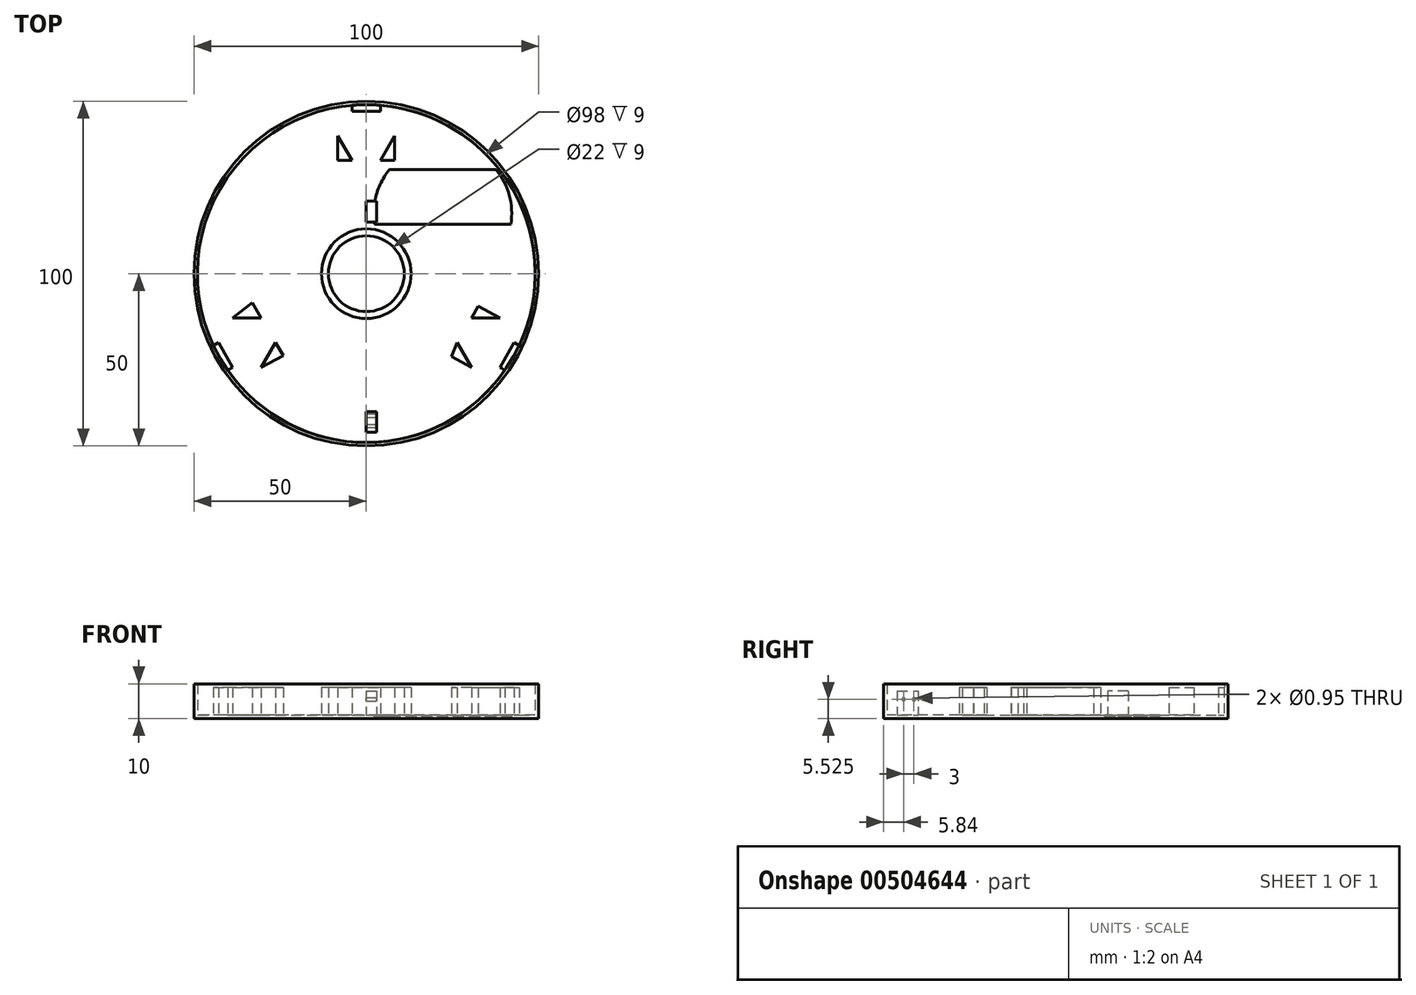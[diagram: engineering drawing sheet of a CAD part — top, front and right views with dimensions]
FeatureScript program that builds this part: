
annotation { "Feature Type Name" : "Feature", "Feature Type Description" : "" }
export const myFeature = defineFeature(function(context is Context, id is Id, definition is map)
    precondition{}
    {
        {
            var Q0;
            Q0=qCreatedBy(makeId("Top.planeOp"),FACE);
            var sketch = newSketch(context, id + "F0", { "sketchPlane" : qUnion([Q0])});
            skCircle(sketch, "E0", {"center": v(0, 0) * mm, "radius": 11 * mm});
            skCircle(sketch, "E1", {"center": v(0, 0) * mm, "radius": 13 * mm});
            skCircle(sketch, "E2", {"center": v(0, 0) * mm, "radius": 50 * mm});
            skCircle(sketch, "E3", {"center": v(0, 0) * mm, "radius": 49 * mm});
            skLineSegment(sketch, "E4.0", {"start": v(113.43, -65.49) * mm, "end": v(-113.43, -65.49) * mm});
            skLineSegment(sketch, "E4.1", {"start": v(-113.43, -65.49) * mm, "end": v(0, 130.97) * mm});
            skLineSegment(sketch, "E4.2", {"start": v(0, 130.97) * mm, "end": v(113.43, -65.49) * mm});
            skPoint(sketch, "E4.0.midPoint", {"position": v(0, -65.49) * mm});
            skLineSegment(sketch, "E5", {"start": v(0, 0) * mm, "end": v(0, 130.97) * mm});
            skLineSegment(sketch, "E6", {"start": v(0, 0) * mm, "end": v(-113.43, -65.49) * mm});
            skLineSegment(sketch, "E7", {"start": v(113.43, -65.49) * mm, "end": v(0, 0) * mm});
            skCircle(sketch, "E8.cCircle", {"center": v(0, 40) * mm, "radius": 7.15 * mm, "construction": true});
            skLineSegment(sketch, "E8.0", {"start": v(4.13, 32.85) * mm, "end": v(-4.13, 32.85) * mm});
            skLineSegment(sketch, "E8.1", {"start": v(-4.13, 32.85) * mm, "end": v(-8.26, 40) * mm});
            skLineSegment(sketch, "E8.2", {"start": v(-8.26, 40) * mm, "end": v(-4.13, 47.15) * mm});
            skLineSegment(sketch, "E8.3", {"start": v(-4.13, 47.15) * mm, "end": v(4.13, 47.15) * mm});
            skLineSegment(sketch, "E8.4", {"start": v(4.13, 47.15) * mm, "end": v(8.26, 40) * mm});
            skLineSegment(sketch, "E8.5", {"start": v(8.26, 40) * mm, "end": v(4.13, 32.85) * mm});
            skPoint(sketch, "E8.0.midPoint", {"position": v(0, 32.85) * mm});
            skCircle(sketch, "E9.cCircle", {"center": v(-34.64, -20) * mm, "radius": 7.15 * mm, "construction": true});
            skLineSegment(sketch, "E9.0", {"start": v(-30.51, -12.85) * mm, "end": v(-26.38, -20) * mm});
            skLineSegment(sketch, "E9.1", {"start": v(-26.38, -20) * mm, "end": v(-30.51, -27.15) * mm});
            skLineSegment(sketch, "E9.2", {"start": v(-30.51, -27.15) * mm, "end": v(-38.77, -27.15) * mm});
            skLineSegment(sketch, "E9.3", {"start": v(-38.77, -27.15) * mm, "end": v(-42.9, -20) * mm});
            skLineSegment(sketch, "E9.4", {"start": v(-42.9, -20) * mm, "end": v(-38.77, -12.85) * mm});
            skLineSegment(sketch, "E9.5", {"start": v(-38.77, -12.85) * mm, "end": v(-30.51, -12.85) * mm});
            skPoint(sketch, "E9.0.midPoint", {"position": v(-28.45, -16.43) * mm});
            skCircle(sketch, "E10.cCircle", {"center": v(34.64, -20) * mm, "radius": 7.15 * mm, "construction": true});
            skLineSegment(sketch, "E10.0", {"start": v(26.38, -20) * mm, "end": v(30.51, -12.85) * mm});
            skLineSegment(sketch, "E10.1", {"start": v(30.51, -12.85) * mm, "end": v(38.77, -12.85) * mm});
            skLineSegment(sketch, "E10.2", {"start": v(38.77, -12.85) * mm, "end": v(42.9, -20) * mm});
            skLineSegment(sketch, "E10.3", {"start": v(42.9, -20) * mm, "end": v(38.77, -27.15) * mm});
            skLineSegment(sketch, "E10.4", {"start": v(38.77, -27.15) * mm, "end": v(30.51, -27.15) * mm});
            skLineSegment(sketch, "E10.5", {"start": v(30.51, -27.15) * mm, "end": v(26.38, -20) * mm});
            skPoint(sketch, "E10.0.midPoint", {"position": v(28.45, -16.43) * mm});
            skLineSegment(sketch, "E11", {"start": v(-4.13, 47.15) * mm, "end": v(-4.13, 48.83) * mm});
            skLineSegment(sketch, "E12", {"start": v(4.13, 47.15) * mm, "end": v(4.13, 48.83) * mm});
            skLineSegment(sketch, "E13", {"start": v(-8.26, 40) * mm, "end": v(-8.26, 32.85) * mm});
            skLineSegment(sketch, "E14", {"start": v(-8.26, 32.85) * mm, "end": v(-4.13, 32.85) * mm});
            skLineSegment(sketch, "E15", {"start": v(8.26, 40) * mm, "end": v(8.26, 32.85) * mm});
            skLineSegment(sketch, "E16", {"start": v(8.26, 32.85) * mm, "end": v(4.13, 32.85) * mm});
            skLineSegment(sketch, "E17", {"start": v(42.9, -20) * mm, "end": v(44.35, -20.84) * mm});
            skLineSegment(sketch, "E18", {"start": v(38.77, -27.15) * mm, "end": v(40.22, -27.99) * mm});
            skLineSegment(sketch, "E19", {"start": v(30.51, -12.85) * mm, "end": v(32.52, -9.37) * mm});
            skLineSegment(sketch, "E20", {"start": v(32.52, -9.37) * mm, "end": v(38.77, -12.85) * mm});
            skLineSegment(sketch, "E21", {"start": v(30.51, -27.15) * mm, "end": v(24.65, -24) * mm});
            skLineSegment(sketch, "E22", {"start": v(24.65, -24) * mm, "end": v(26.38, -20) * mm});
            skLineSegment(sketch, "E23", {"start": v(-42.9, -20) * mm, "end": v(-44.35, -20.84) * mm});
            skLineSegment(sketch, "E24", {"start": v(-38.77, -27.15) * mm, "end": v(-40.22, -27.99) * mm});
            skLineSegment(sketch, "E25", {"start": v(-26.38, -20) * mm, "end": v(-24.13, -23.82) * mm});
            skLineSegment(sketch, "E26", {"start": v(-24.13, -23.82) * mm, "end": v(-30.51, -27.15) * mm});
            skLineSegment(sketch, "E27", {"start": v(-30.51, -12.85) * mm, "end": v(-33.07, -8.43) * mm});
            skLineSegment(sketch, "E28", {"start": v(-33.07, -8.43) * mm, "end": v(-38.77, -12.85) * mm});
            skSolve(sketch);
        }
        {
            var Q0;
            Q0=makeQuery(id+"F0.imprint","IMPRINT",FACE,{"disambiguationData":[TD([[makeQuery(id+"F0.imprint","IMPRINT",EDGE,{"derivedFrom":sQuery(id+"F0.wireOp",EDGE,"E2")}),1.0]])]});
            extrude(context, id + "F1", {"entities" : qUnion([Q0]), "depth" : 10 * mm, "offsetDistance" : 25 * mm});
        }
        {
            var Q0;
            Q0=makeQuery(id+"F0.imprint","IMPRINT",FACE,{"disambiguationData":[TD([[makeQuery(id+"F0.imprint","IMPRINT",EDGE,{"derivedFrom":sQuery(id+"F0.wireOp",EDGE,"E1")}),-1.0]])]});
            var Q1;
            {var subQ0=sQuery(id+"F0.wireOp",EDGE,"E9.4");Q1=makeQuery(id+"F0.imprint","IMPRINT",FACE,{"disambiguationData":[TD([[makeQuery(id+"F0.imprint","IMPRINT",EDGE,{"derivedFrom":subQ0}),-1.0]])]});}
            var Q2;
            {var subQ6=sQuery(id+"F0.wireOp",EDGE,"E9.1");Q2=makeQuery(id+"F0.imprint","IMPRINT",FACE,{"disambiguationData":[TD([[makeQuery(id+"F0.imprint","IMPRINT",EDGE,{"derivedFrom":subQ6}),-1.0]])]});}
            var Q3;
            {var subQ1=sQuery(id+"F0.wireOp",EDGE,"E10.1");Q3=makeQuery(id+"F0.imprint","IMPRINT",FACE,{"disambiguationData":[TD([[makeQuery(id+"F0.imprint","IMPRINT",EDGE,{"derivedFrom":subQ1}),-1.0]])]});}
            var Q4;
            {var subQ0=sQuery(id+"F0.wireOp",EDGE,"E10.4");Q4=makeQuery(id+"F0.imprint","IMPRINT",FACE,{"disambiguationData":[TD([[makeQuery(id+"F0.imprint","IMPRINT",EDGE,{"derivedFrom":subQ0}),-1.0]])]});}
            var Q5;
            {var subQ0=sQuery(id+"F0.wireOp",EDGE,"E8.4");Q5=makeQuery(id+"F0.imprint","IMPRINT",FACE,{"disambiguationData":[TD([[makeQuery(id+"F0.imprint","IMPRINT",EDGE,{"derivedFrom":subQ0}),-1.0]])]});}
            var Q6;
            {var subQ1=sQuery(id+"F0.wireOp",EDGE,"E8.1");Q6=makeQuery(id+"F0.imprint","IMPRINT",FACE,{"disambiguationData":[TD([[makeQuery(id+"F0.imprint","IMPRINT",EDGE,{"derivedFrom":subQ1}),-1.0]])]});}
            extrude(context, id + "F2", {"entities" : qUnion([Q0, Q1, Q2, Q3, Q4, Q5, Q6]), "operationType" : NewBodyOperationType.ADD, "depth" : 1 * mm, "offsetDistance" : 25 * mm});
        }
        {
            var Q0;
            Q0=makeQuery(id+"F0.imprint","IMPRINT",FACE,{"disambiguationData":[TD([[makeQuery(id+"F0.imprint","IMPRINT",EDGE,{"derivedFrom":sQuery(id+"F0.wireOp",EDGE,"E0")}),-1.0]])]});
            var Q1;
            Q1=makeQuery(id+"F0.imprint","IMPRINT",FACE,{"disambiguationData":[TD([[makeQuery(id+"F0.imprint","IMPRINT",EDGE,{"derivedFrom":sQuery(id+"F0.wireOp",EDGE,"E9.1")}),1.0]])]});
            var Q2;
            {var subQ0=sQuery(id+"F0.wireOp",EDGE,"E24");Q2=makeQuery(id+"F0.imprint","IMPRINT",FACE,{"disambiguationData":[TD([[makeQuery(id+"F0.imprint","IMPRINT",EDGE,{"derivedFrom":subQ0}),-1.0]])]});}
            var Q3;
            {var subQ0=sQuery(id+"F0.wireOp",EDGE,"E23");Q3=makeQuery(id+"F0.imprint","IMPRINT",FACE,{"disambiguationData":[TD([[makeQuery(id+"F0.imprint","IMPRINT",EDGE,{"derivedFrom":subQ0}),1.0]])]});}
            var Q4;
            Q4=makeQuery(id+"F0.imprint","IMPRINT",FACE,{"disambiguationData":[TD([[makeQuery(id+"F0.imprint","IMPRINT",EDGE,{"derivedFrom":sQuery(id+"F0.wireOp",EDGE,"E9.5")}),1.0]])]});
            var Q5;
            Q5=makeQuery(id+"F0.imprint","IMPRINT",FACE,{"disambiguationData":[TD([[makeQuery(id+"F0.imprint","IMPRINT",EDGE,{"derivedFrom":sQuery(id+"F0.wireOp",EDGE,"E8.5")}),1.0]])]});
            var Q6;
            Q6=makeQuery(id+"F0.imprint","IMPRINT",FACE,{"disambiguationData":[TD([[makeQuery(id+"F0.imprint","IMPRINT",EDGE,{"derivedFrom":sQuery(id+"F0.wireOp",EDGE,"E8.1")}),1.0]])]});
            var Q7;
            {var subQ0=sQuery(id+"F0.wireOp",EDGE,"E12");Q7=makeQuery(id+"F0.imprint","IMPRINT",FACE,{"disambiguationData":[TD([[makeQuery(id+"F0.imprint","IMPRINT",EDGE,{"derivedFrom":subQ0}),1.0]])]});}
            var Q8;
            {var subQ0=sQuery(id+"F0.wireOp",EDGE,"E11");Q8=makeQuery(id+"F0.imprint","IMPRINT",FACE,{"disambiguationData":[TD([[makeQuery(id+"F0.imprint","IMPRINT",EDGE,{"derivedFrom":subQ0}),-1.0]])]});}
            var Q9;
            Q9=makeQuery(id+"F0.imprint","IMPRINT",FACE,{"disambiguationData":[TD([[makeQuery(id+"F0.imprint","IMPRINT",EDGE,{"derivedFrom":sQuery(id+"F0.wireOp",EDGE,"E10.5")}),1.0]])]});
            var Q10;
            Q10=makeQuery(id+"F0.imprint","IMPRINT",FACE,{"disambiguationData":[TD([[makeQuery(id+"F0.imprint","IMPRINT",EDGE,{"derivedFrom":sQuery(id+"F0.wireOp",EDGE,"E10.1")}),1.0]])]});
            var Q11;
            {var subQ0=sQuery(id+"F0.wireOp",EDGE,"E17");Q11=makeQuery(id+"F0.imprint","IMPRINT",FACE,{"disambiguationData":[TD([[makeQuery(id+"F0.imprint","IMPRINT",EDGE,{"derivedFrom":subQ0}),-1.0]])]});}
            var Q12;
            {var subQ0=sQuery(id+"F0.wireOp",EDGE,"E18");Q12=makeQuery(id+"F0.imprint","IMPRINT",FACE,{"disambiguationData":[TD([[makeQuery(id+"F0.imprint","IMPRINT",EDGE,{"derivedFrom":subQ0}),1.0]])]});}
            extrude(context, id + "F3", {"entities" : qUnion([Q0, Q1, Q2, Q3, Q4, Q5, Q6, Q7, Q8, Q9, Q10, Q11, Q12]), "operationType" : NewBodyOperationType.ADD, "depth" : 9 * mm, "offsetDistance" : 25 * mm});
        }
        {
            var Q0;
            Q0=makeQuery(id+"F2.opExtrude","CAP_FACE",FACE,{"disambiguationData":[OSD([sQuery(id+"F0.wireOp",EDGE,"E1"),sQuery(id+"F0.wireOp",EDGE,"E3"),sQuery(id+"F0.wireOp",EDGE,"E8.1"),sQuery(id+"F0.wireOp",EDGE,"E8.3"),sQuery(id+"F0.wireOp",EDGE,"E8.5"),sQuery(id+"F0.wireOp",EDGE,"E9.1"),sQuery(id+"F0.wireOp",EDGE,"E9.3"),sQuery(id+"F0.wireOp",EDGE,"E9.5"),sQuery(id+"F0.wireOp",EDGE,"E10.1"),sQuery(id+"F0.wireOp",EDGE,"E10.3"),sQuery(id+"F0.wireOp",EDGE,"E10.5"),sQuery(id+"F0.wireOp",EDGE,"E11"),sQuery(id+"F0.wireOp",EDGE,"E12"),sQuery(id+"F0.wireOp",EDGE,"E13"),sQuery(id+"F0.wireOp",EDGE,"E14"),sQuery(id+"F0.wireOp",EDGE,"E15"),sQuery(id+"F0.wireOp",EDGE,"E16"),sQuery(id+"F0.wireOp",EDGE,"E17"),sQuery(id+"F0.wireOp",EDGE,"E18"),sQuery(id+"F0.wireOp",EDGE,"E19"),sQuery(id+"F0.wireOp",EDGE,"E20"),sQuery(id+"F0.wireOp",EDGE,"E21"),sQuery(id+"F0.wireOp",EDGE,"E22"),sQuery(id+"F0.wireOp",EDGE,"E23"),sQuery(id+"F0.wireOp",EDGE,"E24"),sQuery(id+"F0.wireOp",EDGE,"E25"),sQuery(id+"F0.wireOp",EDGE,"E26"),sQuery(id+"F0.wireOp",EDGE,"E27"),sQuery(id+"F0.wireOp",EDGE,"E28")])],"isStart":false});
            var sketch = newSketch(context, id + "F4", { "sketchPlane" : qUnion([Q0])});
            skLineSegment(sketch, "E29.bottom", {"start": v(0, -46) * mm, "end": v(3, -46) * mm});
            skLineSegment(sketch, "E29.top", {"start": v(0, -40) * mm, "end": v(3, -40) * mm});
            skLineSegment(sketch, "E29.left", {"start": v(0, -46) * mm, "end": v(0, -40) * mm});
            skLineSegment(sketch, "E29.right", {"start": v(3, -46) * mm, "end": v(3, -40) * mm});
            skLineSegment(sketch, "E30.bottom", {"start": v(0, 21) * mm, "end": v(3, 21) * mm});
            skLineSegment(sketch, "E30.top", {"start": v(0, 15) * mm, "end": v(3, 15) * mm});
            skLineSegment(sketch, "E30.left", {"start": v(0, 21) * mm, "end": v(0, 15) * mm});
            skLineSegment(sketch, "E30.right", {"start": v(3, 21) * mm, "end": v(3, 15) * mm});
            skSolve(sketch);
        }
        {
            var Q0;
            Q0=makeQuery(id+"F4.imprint","IMPRINT",FACE,{"disambiguationData":[TD([[makeQuery(id+"F4.imprint","IMPRINT",EDGE,{"derivedFrom":sQuery(id+"F4.wireOp",EDGE,"E29.bottom")}),1.0]])]});
            var Q1;
            Q1=makeQuery(id+"F4.imprint","IMPRINT",FACE,{"disambiguationData":[TD([[makeQuery(id+"F4.imprint","IMPRINT",EDGE,{"derivedFrom":sQuery(id+"F4.wireOp",EDGE,"E30.bottom")}),-1.0]])]});
            extrude(context, id + "F5", {"entities" : qUnion([Q0, Q1]), "operationType" : NewBodyOperationType.ADD, "depth" : 7 * mm, "offsetDistance" : 25 * mm});
        }
        {
            var Q0;
            Q0=makeQuery(id+"F5.opExtrude","SWEPT_FACE",FACE,{"disambiguationData":[OSD([sQuery(id+"F4.wireOp",EDGE,"E29.right")])]});
            var sketch = newSketch(context, id + "F6", { "sketchPlane" : qUnion([Q0])});
            skCircle(sketch, "E31", {"center": v(-41.16, 5.53) * mm, "radius": 0.48 * mm});
            skCircle(sketch, "E32", {"center": v(-44.16, 5.53) * mm, "radius": 0.47 * mm});
            skSolve(sketch);
        }
        {
            var Q0;
            Q0=makeQuery(id+"F5.opExtrude","SWEPT_FACE",FACE,{"disambiguationData":[OSD([sQuery(id+"F4.wireOp",EDGE,"E30.right")])]});
            var sketch = newSketch(context, id + "F7", { "sketchPlane" : qUnion([Q0])});
            skCircle(sketch, "E33", {"center": v(26.47, 6.58) * mm, "radius": 0.47 * mm});
            skCircle(sketch, "E34", {"center": v(29.47, 6.58) * mm, "radius": 0.47 * mm});
            skSolve(sketch);
        }
        {
            var Q0;
            Q0=makeQuery(id+"F7.imprint","IMPRINT",FACE,{"disambiguationData":[TD([[makeQuery(id+"F7.imprint","IMPRINT",EDGE,{"derivedFrom":sQuery(id+"F7.wireOp",EDGE,"E33")}),1.0]])]});
            var Q1;
            Q1=makeQuery(id+"F7.imprint","IMPRINT",FACE,{"disambiguationData":[TD([[makeQuery(id+"F7.imprint","IMPRINT",EDGE,{"derivedFrom":sQuery(id+"F7.wireOp",EDGE,"E34")}),1.0]])]});
            var Q2;
            Q2=makeQuery(id+"F6.imprint","IMPRINT",FACE,{"disambiguationData":[TD([[makeQuery(id+"F6.imprint","IMPRINT",EDGE,{"derivedFrom":sQuery(id+"F6.wireOp",EDGE,"E32")}),1.0]])]});
            var Q3;
            Q3=makeQuery(id+"F6.imprint","IMPRINT",FACE,{"disambiguationData":[TD([[makeQuery(id+"F6.imprint","IMPRINT",EDGE,{"derivedFrom":sQuery(id+"F6.wireOp",EDGE,"E31")}),1.0]])]});
            extrude(context, id + "F8", {"entities" : qUnion([Q0, Q1, Q2, Q3]), "operationType" : NewBodyOperationType.REMOVE, "oppositeDirection" : true, "depth" : 3 * mm, "offsetDistance" : 25 * mm});
        }
        {
            var Q0;
            Q0=makeQuery(id+"F2.opExtrude","CAP_FACE",FACE,{"disambiguationData":[OSD([sQuery(id+"F0.wireOp",EDGE,"E1"),sQuery(id+"F0.wireOp",EDGE,"E3"),sQuery(id+"F0.wireOp",EDGE,"E8.1"),sQuery(id+"F0.wireOp",EDGE,"E8.3"),sQuery(id+"F0.wireOp",EDGE,"E8.5"),sQuery(id+"F0.wireOp",EDGE,"E9.1"),sQuery(id+"F0.wireOp",EDGE,"E9.3"),sQuery(id+"F0.wireOp",EDGE,"E9.5"),sQuery(id+"F0.wireOp",EDGE,"E10.1"),sQuery(id+"F0.wireOp",EDGE,"E10.3"),sQuery(id+"F0.wireOp",EDGE,"E10.5"),sQuery(id+"F0.wireOp",EDGE,"E11"),sQuery(id+"F0.wireOp",EDGE,"E12"),sQuery(id+"F0.wireOp",EDGE,"E13"),sQuery(id+"F0.wireOp",EDGE,"E14"),sQuery(id+"F0.wireOp",EDGE,"E15"),sQuery(id+"F0.wireOp",EDGE,"E16"),sQuery(id+"F0.wireOp",EDGE,"E17"),sQuery(id+"F0.wireOp",EDGE,"E18"),sQuery(id+"F0.wireOp",EDGE,"E19"),sQuery(id+"F0.wireOp",EDGE,"E20"),sQuery(id+"F0.wireOp",EDGE,"E21"),sQuery(id+"F0.wireOp",EDGE,"E22"),sQuery(id+"F0.wireOp",EDGE,"E23"),sQuery(id+"F0.wireOp",EDGE,"E24"),sQuery(id+"F0.wireOp",EDGE,"E25"),sQuery(id+"F0.wireOp",EDGE,"E26"),sQuery(id+"F0.wireOp",EDGE,"E27"),sQuery(id+"F0.wireOp",EDGE,"E28")])],"isStart":false});
            var sketch = newSketch(context, id + "F9", { "sketchPlane" : qUnion([Q0])});
            skLineSegment(sketch, "E35.bottom", {"start": v(2.48, 21.05) * mm, "end": v(-7.02, 21.05) * mm});
            skLineSegment(sketch, "E35.top", {"start": v(2.48, 28.55) * mm, "end": v(-7.02, 28.55) * mm});
            skLineSegment(sketch, "E35.left", {"start": v(2.48, 21.05) * mm, "end": v(2.48, 28.55) * mm});
            skLineSegment(sketch, "E35.right", {"start": v(-7.02, 21.05) * mm, "end": v(-7.02, 28.55) * mm});
            skCircle(sketch, "E36", {"center": v(22.18, 17.49) * mm, "radius": 19 * mm});
            skCircle(sketch, "E37", {"center": v(22.18, 17.49) * mm, "radius": 20 * mm});
            skLineSegment(sketch, "E38", {"start": v(6.73, 28.55) * mm, "end": v(37.63, 28.55) * mm});
            skLineSegment(sketch, "E39", {"start": v(6.73, 30.19) * mm, "end": v(37.63, 30.19) * mm});
            skLineSegment(sketch, "E40", {"start": v(3.24, 16.05) * mm, "end": v(41.13, 16.05) * mm});
            skLineSegment(sketch, "E41", {"start": v(2.43, 14.34) * mm, "end": v(41.93, 14.34) * mm});
            skSolve(sketch);
        }
        {
            var Q0;
            {var subQ0=sQuery(id+"F9.wireOp",EDGE,"E38");Q0=makeQuery(id+"F9.imprint","IMPRINT",FACE,{"disambiguationData":[TD([[makeQuery(id+"F9.imprint","IMPRINT",EDGE,{"derivedFrom":subQ0}),1.0]])]});}
            var Q1;
            {var subQ5=sQuery(id+"F9.wireOp",EDGE,"E36");var subQ8=makeQuery(id+"F9.imprint","INTERSECT",VERTEX,{"disambiguationData":[OD(0.0)],"derivedFrom":[subQ5,sQuery(id+"F9.wireOp",EDGE,"E38")]});Q1=makeQuery(id+"F9.imprint","IMPRINT",FACE,{"disambiguationData":[TD([[makeQuery(id+"F9.imprint","IMPRINT",EDGE,{"disambiguationData":[TD([[subQ8,1.0]])],"derivedFrom":subQ5}),-1.0]])]});}
            var Q2;
            {var subQ0=sQuery(id+"F9.wireOp",EDGE,"E40");Q2=makeQuery(id+"F9.imprint","IMPRINT",FACE,{"disambiguationData":[TD([[makeQuery(id+"F9.imprint","IMPRINT",EDGE,{"derivedFrom":subQ0}),-1.0]])]});}
            var Q3;
            {var subQ0=sQuery(id+"F9.wireOp",EDGE,"E36");var subQ1=makeQuery(id+"F9.imprint","INTERSECT",VERTEX,{"disambiguationData":[OD(1.0)],"derivedFrom":[subQ0,sQuery(id+"F9.wireOp",EDGE,"E38")]});Q3=makeQuery(id+"F9.imprint","IMPRINT",FACE,{"disambiguationData":[TD([[makeQuery(id+"F9.imprint","IMPRINT",EDGE,{"disambiguationData":[TD([[subQ1,-1.0]])],"derivedFrom":subQ0}),-1.0]])]});}
            var Q4;
            {var subQ0=sQuery(id+"F9.wireOp",EDGE,"E38");Q4=makeQuery(id+"F9.imprint","IMPRINT",FACE,{"disambiguationData":[TD([[makeQuery(id+"F9.imprint","IMPRINT",EDGE,{"derivedFrom":subQ0}),-1.0]])]});}
            extrude(context, id + "F10", {"entities" : qUnion([Q0, Q1, Q2, Q3, Q4]), "operationType" : NewBodyOperationType.REMOVE, "oppositeDirection" : true, "depth" : .5 * mm, "offsetDistance" : 25 * mm});
        }
    });
